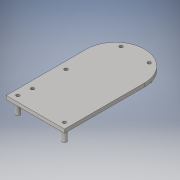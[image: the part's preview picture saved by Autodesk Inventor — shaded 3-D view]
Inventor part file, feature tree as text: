
AUTODESK INVENTOR PART (.ipt)
format: ipt  version: 2016 (Build 200138000, 138)  size: 133,632 bytes
history: native  units: in
note: dims shown in document units (in); Inventor stores cm internally (conversion verified against a paired STEP export)
features: sketch x4, extrude x2, hole x2
ambient origin geometry x8: Origin, YZ Plane, XZ Plane, XY Plane, X Axis, Y Axis, Z Axis, Center Point
bodies: Solid1 (feature_tree)
feature tree (8):
  extrude  "Extrusion1"  Depth=3.1496in
  hole  "Hole1"  [1 undecoded]
  extrude  "Extrusion2"  Depth=0.3937in
  hole  "Hole3"  [1 undecoded]
  sketch  "Sketch2"  dims[d3=4.3307in d4=3.1496in]
  sketch  "Sketch3"  dims[d5=0.1969in d6=0.0in]
  sketch  "Sketch5"  dims[d17=0.1772in d18=0.2362in d19=0.3701in d20=0.0787in d21=90.0deg d22=0.315in d23=0.8108in d34=0.315in]
  sketch  "Sketch7"  dims[d35=0.315in d41=0.315in d43=0.6693in d44=0.0in d52=0.2362in d53=0.2362in d68=0.1772in d69=0.2362in d70=0.3701in d71=0.0787in d72=90.0deg d73=0.315in d74=0.8108in d75=1.5748in d78=1.0286in d79=0.3937in d80=1.811in]
note: 2 required parameter values undecoded (feature->parameter linkage not recoverable at this tier; creation-order binding heuristic only, values carry confidence <= 0.55)
